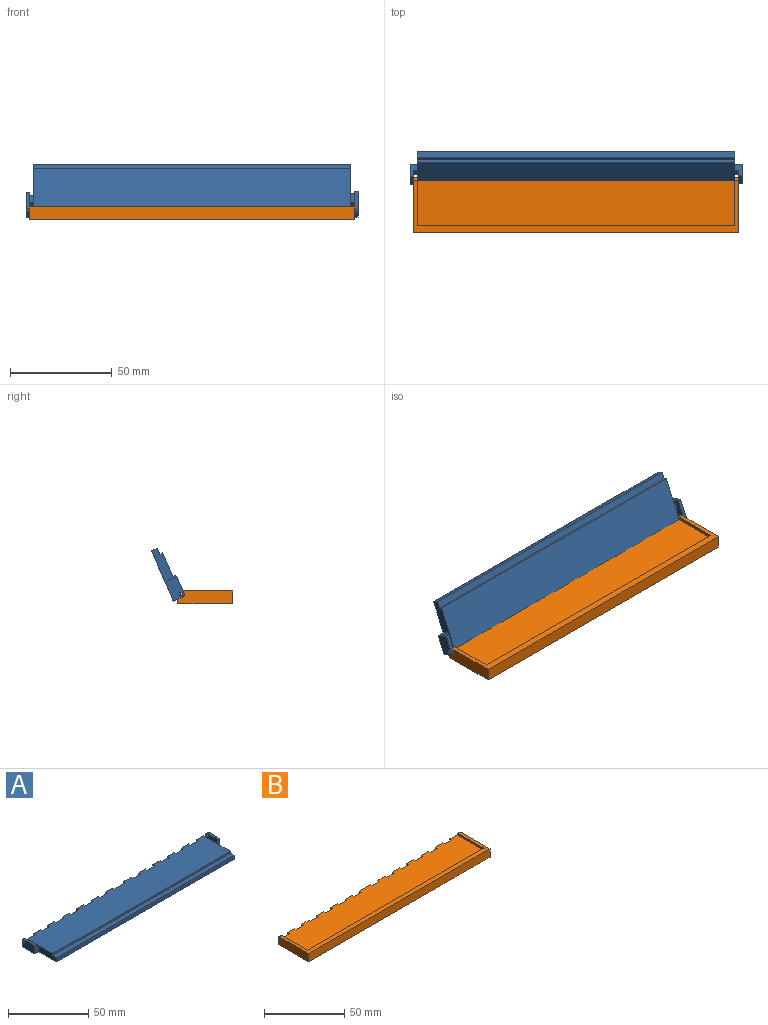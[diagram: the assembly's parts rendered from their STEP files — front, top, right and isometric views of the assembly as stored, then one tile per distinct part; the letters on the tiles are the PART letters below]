
ASSEMBLY  parts=2 mates=1
PART A: 61 faces, bbox 163.1x27x6.3 mm
  f0: plane 26.97x4.75mm, normal (1,0,0), area 104.8mm2, adj f12,f13,f15,f16,f17,f41,f42,f43
  f1: cylinder r=1.57mm len=6.35mm, axis (1,0,0), area 15.7mm2, adj f13,f15,f39,f40
  f2: cylinder r=1.57mm len=6.35mm, axis (1,0,0), area 15.7mm2, adj f13,f15,f37,f38
  f3: cylinder r=1.57mm len=6.35mm, axis (1,0,0), area 15.7mm2, adj f13,f15,f35,f36
  f4: cylinder r=1.57mm len=6.35mm, axis (1,0,0), area 15.7mm2, adj f13,f15,f33,f34
  f5: cylinder r=1.57mm len=6.35mm, axis (1,0,0), area 15.7mm2, adj f13,f15,f31,f32
  f6: cylinder r=1.57mm len=6.35mm, axis (1,0,0), area 15.7mm2, adj f13,f15,f29,f30
  f7: cylinder r=1.57mm len=6.35mm, axis (1,0,0), area 15.7mm2, adj f13,f15,f26,f28
  f8: cylinder r=1.57mm len=6.35mm, axis (1,0,0), area 15.7mm2, adj f13,f15,f24,f27
  f9: cylinder r=1.57mm len=6.35mm, axis (1,0,0), area 15.7mm2, adj f13,f15,f22,f25
  f10: cylinder r=1.57mm len=6.35mm, axis (1,0,0), area 15.7mm2, adj f13,f15,f20,f23
  f11: cylinder r=1.57mm len=6.35mm, axis (1,0,0), area 15.7mm2, adj f13,f15,f18,f21
  f12: cylinder r=1.57mm len=6.35mm, axis (1,0,0), area 15.7mm2, adj f0,f13,f15,f19
  f13: plane 155.96x23.67mm, normal (0,0,1), area 3566.3mm2, adj f0,f1,f2,f3,f4,f5,f6,f7
  f14: plane 25.4x4.75mm, normal (-1,0,0), area 100.4mm2, adj f13,f15,f16,f17,f41,f42,f46,f47
  f15: plane 155.96x4.75mm, normal (0,1,0), area 620.8mm2, adj f0,f1,f2,f3,f4,f5,f6,f7
  f16: plane 155.96x3.18mm, normal (0,-1,0), area 495.2mm2, adj f0,f14,f17,f42
  f17: plane 163.07x26.97mm, normal (0,0,-1), area 4012.2mm2, adj f0,f14,f15,f16,f43,f45,f46,f48
  f18: plane 1.58x1.58mm, normal (1,0,0), area 1.9mm2, adj f11,f13,f15
  f19: plane 1.58x1.58mm, normal (-1,0,0), area 1.9mm2, adj f12,f13,f15
  f20: plane 1.58x1.58mm, normal (1,0,0), area 1.9mm2, adj f10,f13,f15
  f21: plane 1.58x1.58mm, normal (-1,0,0), area 1.9mm2, adj f11,f13,f15
  f22: plane 1.58x1.58mm, normal (1,0,0), area 1.9mm2, adj f9,f13,f15
  f23: plane 1.58x1.58mm, normal (-1,0,0), area 1.9mm2, adj f10,f13,f15
  f24: plane 1.58x1.58mm, normal (1,0,0), area 1.9mm2, adj f8,f13,f15
  f25: plane 1.58x1.58mm, normal (-1,0,0), area 1.9mm2, adj f9,f13,f15
  f26: plane 1.58x1.58mm, normal (1,0,0), area 1.9mm2, adj f7,f13,f15
  f27: plane 1.58x1.58mm, normal (-1,0,0), area 1.9mm2, adj f8,f13,f15
  f28: plane 1.58x1.58mm, normal (-1,0,0), area 1.9mm2, adj f7,f13,f15
  f29: plane 1.58x1.57mm, normal (1,0,0), area 1.9mm2, adj f6,f13,f15
  f30: plane 1.58x1.57mm, normal (-1,0,0), area 1.9mm2, adj f6,f13,f15
  f31: plane 1.58x1.57mm, normal (1,0,0), area 1.9mm2, adj f5,f13,f15
  f32: plane 1.58x1.57mm, normal (-1,0,0), area 1.9mm2, adj f5,f13,f15
  f33: plane 1.58x1.58mm, normal (1,0,0), area 1.9mm2, adj f4,f13,f15
  f34: plane 1.58x1.58mm, normal (-1,0,0), area 1.9mm2, adj f4,f13,f15
  f35: plane 1.58x1.58mm, normal (1,0,0), area 1.9mm2, adj f3,f13,f15
  f36: plane 1.58x1.58mm, normal (-1,0,0), area 1.9mm2, adj f3,f13,f15
  f37: plane 1.58x1.58mm, normal (1,0,0), area 1.9mm2, adj f2,f13,f15
  f38: plane 1.58x1.58mm, normal (-1,0,0), area 1.9mm2, adj f2,f13,f15
  f39: plane 1.58x1.58mm, normal (1,0,0), area 1.9mm2, adj f1,f13,f15
  f40: plane 1.58x1.58mm, normal (-1,0,0), area 1.9mm2, adj f1,f13,f15
  f41: plane 155.96x1.57mm, normal (0,-1,0), area 245.6mm2, adj f0,f13,f14,f42
  f42: plane 155.96x3.3mm, normal (0,0,1), area 515mm2, adj f0,f14,f16,f41
  f43: plane 3.19x1.98mm, normal (0,1,0), area 6.3mm2, adj f0,f17,f44,f58
  f44: plane 3.95x1.98mm, normal (0,0,1), area 7.8mm2, adj f0,f43,f45,f58
  f45: plane 6.32x3.56mm, normal (0,-1,0), area 16.3mm2, adj f0,f17,f44,f56,f57,f58
  f46: plane 6.22x3.56mm, normal (0,-1,0), area 16.1mm2, adj f14,f17,f47,f49,f52,f53
  f47: plane 4.75x1.98mm, normal (0,0,1), area 9.4mm2, adj f14,f46,f48,f53
  f48: plane 3.18x1.98mm, normal (0,1,0), area 6.3mm2, adj f14,f17,f47,f53
  f49: plane 9.5x1.57mm, normal (0,0,1), area 15mm2, adj f46,f50,f52,f53
  f50: cylinder r=1.57mm len=1.57mm, axis (1,0,0), area 3.9mm2, adj f49,f51,f52,f53
  f51: plane 4.64x1.57mm, normal (0,1,0), area 7.3mm2, adj f17,f50,f52,f53
  f52: plane 11.07x6.22mm, normal (-1,0,0), area 66.3mm2, adj f17,f46,f49,f50,f51,f60
  f53: plane 11.07x6.22mm, normal (1,0,0), area 51.2mm2, adj f17,f46,f47,f48,f49,f50,f51,f60
  f54: plane 4.75x1.57mm, normal (0,1,0), area 7.5mm2, adj f17,f55,f57,f58
  f55: cylinder r=1.57mm len=1.58mm, axis (-1,0,0), area 3.9mm2, adj f54,f56,f57,f58
  f56: plane 8.7x1.57mm, normal (0,0,1), area 13.7mm2, adj f45,f55,f57,f58
  f57: plane 10.28x6.32mm, normal (1,0,0), area 62.5mm2, adj f17,f45,f54,f55,f56,f59
  f58: plane 10.28x6.32mm, normal (-1,0,0), area 49.8mm2, adj f17,f43,f44,f45,f54,f55,f56,f59
  f59: cylinder r=0.8mm len=1.6mm, axis (-1,0,0), area 7.9mm2, adj f57,f58
  f60: cylinder r=0.8mm len=1.6mm, axis (1,0,0), area 7.9mm2, adj f52,f53
PART B: 54 faces, bbox 159.9x27x6.3 mm
  f0: cylinder r=1.57mm len=6.35mm, axis (1,0,0), area 15.7mm2, adj f12,f13,f37,f38
  f1: cylinder r=1.57mm len=6.35mm, axis (1,0,0), area 15.7mm2, adj f12,f13,f35,f36
  f2: cylinder r=1.57mm len=6.35mm, axis (1,0,0), area 15.7mm2, adj f12,f13,f33,f34
  f3: cylinder r=1.57mm len=6.35mm, axis (1,0,0), area 15.7mm2, adj f12,f13,f31,f32
  f4: cylinder r=1.57mm len=6.35mm, axis (1,0,0), area 15.7mm2, adj f12,f13,f29,f30
  f5: cylinder r=1.57mm len=9.91mm, axis (1,0,0), area 24.5mm2, adj f12,f13,f27,f28
  f6: cylinder r=1.57mm len=6.35mm, axis (1,0,0), area 15.7mm2, adj f12,f13,f24,f26
  f7: cylinder r=1.57mm len=6.35mm, axis (1,0,0), area 15.7mm2, adj f12,f13,f22,f25
  f8: cylinder r=1.57mm len=6.35mm, axis (1,0,0), area 15.7mm2, adj f12,f13,f20,f23
  f9: cylinder r=1.57mm len=6.35mm, axis (1,0,0), area 15.7mm2, adj f12,f13,f18,f21
  f10: cylinder r=1.57mm len=6.35mm, axis (1,0,0), area 15.7mm2, adj f12,f13,f16,f19
  f11: cylinder r=1.57mm len=6.35mm, axis (1,0,0), area 15.7mm2, adj f12,f13,f17,f41
  f12: plane 155.96x23.67mm, normal (0,0,1), area 3571.9mm2, adj f0,f1,f2,f3,f4,f5,f6,f7
  f13: plane 155.96x4.75mm, normal (0,1,0), area 615.2mm2, adj f0,f1,f2,f3,f4,f5,f6,f7
  f14: plane 159.92x6.32mm, normal (0,-1,0), area 1011.4mm2, adj f15,f40,f45,f49
  f15: plane 159.92x26.97mm, normal (0,0,-1), area 4068.2mm2, adj f13,f14,f41,f43,f45,f46,f48,f49
  f16: plane 1.58x1.58mm, normal (1,0,0), area 1.9mm2, adj f10,f12,f13
  f17: plane 1.58x1.58mm, normal (-1,0,0), area 1.9mm2, adj f11,f12,f13
  f18: plane 1.58x1.58mm, normal (1,0,0), area 1.9mm2, adj f9,f12,f13
  f19: plane 1.58x1.58mm, normal (-1,0,0), area 1.9mm2, adj f10,f12,f13
  f20: plane 1.58x1.58mm, normal (1,0,0), area 1.9mm2, adj f8,f12,f13
  f21: plane 1.58x1.58mm, normal (-1,0,0), area 1.9mm2, adj f9,f12,f13
  f22: plane 1.58x1.58mm, normal (1,0,0), area 1.9mm2, adj f7,f12,f13
  f23: plane 1.58x1.58mm, normal (-1,0,0), area 1.9mm2, adj f8,f12,f13
  f24: plane 1.58x1.58mm, normal (1,0,0), area 1.9mm2, adj f6,f12,f13
  f25: plane 1.58x1.58mm, normal (-1,0,0), area 1.9mm2, adj f7,f12,f13
  f26: plane 1.58x1.58mm, normal (-1,0,0), area 1.9mm2, adj f6,f12,f13
  f27: plane 1.58x1.57mm, normal (1,0,0), area 1.9mm2, adj f5,f12,f13
  f28: plane 1.58x1.57mm, normal (-1,0,0), area 1.9mm2, adj f5,f12,f13
  f29: plane 1.58x1.57mm, normal (1,0,0), area 1.9mm2, adj f4,f12,f13
  f30: plane 1.58x1.57mm, normal (-1,0,0), area 1.9mm2, adj f4,f12,f13
  f31: plane 1.58x1.58mm, normal (1,0,0), area 1.9mm2, adj f3,f12,f13
  f32: plane 1.58x1.58mm, normal (-1,0,0), area 1.9mm2, adj f3,f12,f13
  f33: plane 1.58x1.58mm, normal (1,0,0), area 1.9mm2, adj f2,f12,f13
  f34: plane 1.58x1.58mm, normal (-1,0,0), area 1.9mm2, adj f2,f12,f13
  f35: plane 1.58x1.58mm, normal (1,0,0), area 1.9mm2, adj f1,f12,f13
  f36: plane 1.58x1.58mm, normal (-1,0,0), area 1.9mm2, adj f1,f12,f13
  f37: plane 1.58x1.58mm, normal (1,0,0), area 1.9mm2, adj f0,f12,f13
  f38: plane 1.58x1.58mm, normal (-1,0,0), area 1.9mm2, adj f0,f12,f13
  f39: plane 155.96x1.57mm, normal (0,1,0), area 245.6mm2, adj f12,f40,f42,f46
  f40: plane 159.92x25.4mm, normal (0,0,1), area 615.6mm2, adj f14,f39,f42,f44,f45,f46,f47,f49
  f41: plane 4.75x1.57mm, normal (-1,0,0), area 5.5mm2, adj f11,f13,f15,f43
  f42: plane 23.67x1.57mm, normal (-1,0,0), area 35.8mm2, adj f12,f39,f40,f44,f52
  f43: plane 4.75x1.98mm, normal (0,1,0), area 9.4mm2, adj f15,f41,f44,f45
  f44: cylinder r=1.57mm len=1.98mm, axis (-1,0,0), area 4.9mm2, adj f40,f42,f43,f45
  f45: plane 26.97x6.32mm, normal (1,0,0), area 168.1mm2, adj f14,f15,f40,f43,f44,f52
  f46: plane 23.67x6.32mm, normal (1,0,0), area 42.8mm2, adj f12,f13,f15,f39,f40,f47,f48,f51
  f47: cylinder r=1.57mm len=1.98mm, axis (1,0,0), area 4.9mm2, adj f40,f46,f48,f49
  f48: plane 4.75x1.98mm, normal (0,1,0), area 9.4mm2, adj f15,f46,f47,f49
  f49: plane 26.97x6.32mm, normal (-1,0,0), area 168.1mm2, adj f14,f15,f40,f47,f48,f51
  f50: plane 0.79x0.79mm, normal (-1,0,0), area 0.5mm2, adj f12,f13,f51
  f51: cylinder r=0.79mm len=1.98mm, axis (-1,0,0), area 9.8mm2, adj f46,f49,f50
  f52: cylinder r=0.79mm len=1.98mm, axis (1,0,0), area 9.8mm2, adj f42,f45,f53
  f53: plane 1.57x0.79mm, normal (1,0,0), area 1mm2, adj f12,f52
PLACE A rot(axis=(0,-0.55,0.84),180deg) t=(-129.32,8.57,41.83)mm
PLACE B t=(26.64,8.57,41.83)mm fixed
MATE revolute A.f1 <-> B.f0  axis (-1,0,0) through (-129.32,8.57,41.83)mm
